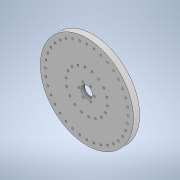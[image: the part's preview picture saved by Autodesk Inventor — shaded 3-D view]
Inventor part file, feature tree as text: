
AUTODESK INVENTOR PART (.ipt)
format: ipt  version: 2020.3 (Build 243373000, 373)  size: 738,304 bytes
history: native  units: mm
features: extrude x12, sketch x12, pattern_circular x4, mirror x1
ambient origin geometry x8: Origin, YZ Plane, XZ Plane, XY Plane, X Axis, Y Axis, Z Axis, Center Point
bodies: Solid1 (feature_tree)
feature tree (29):
  extrude  "Extrusion1"  Depth=40.0mm
  extrude  "Extrusion2"  Depth=7.0mm
  extrude  "Extrusion3"  Depth=180.0mm
  extrude  "Extrusion4"  Depth=5.0mm
  extrude  "Extrusion5"  Depth=7.0mm
  mirror  "Mirror1"
  pattern_circular  "Circular Pattern1"  Count=60 Angle=360.0deg
  extrude  "Extrusion6"  Depth=60.0mm
  pattern_circular  "Circular Pattern2"  [2 undecoded]
  extrude  "Extrusion7"  Depth=60.0mm TaperAngle=360.0deg
  extrude  "Extrusion8"  Depth=60.0mm
  extrude  "Extrusion10"  Depth=60.0mm TaperAngle=0.0deg
  pattern_circular  "Circular Pattern4"  [2 undecoded]
  extrude  "Extrusion12"  Depth=60.0mm
  extrude  "Extrusion13"  Depth=60.0mm
  pattern_circular  "Circular Pattern5"  [2 undecoded]
  extrude  "Extrusion14"  Depth=60.0mm
  sketch  "Sketch1"  dims[d0=40.0mm d1=22.0mm]
  sketch  "Sketch2"  dims[d2=7.0mm d3=0.0mm d4=8.6mm]
  sketch  "Sketch3"  dims[d5=16.0mm d6=0.0mm d7=180.0mm]
  sketch  "Sketch4"  dims[d8=5.0mm d9=0.0mm d10=22.0mm]
  sketch  "Sketch5"  dims[d11=7.0mm d12=0.0mm d14=0.55mm]
  sketch  "Sketch6"  dims[d17=0.4mm]
  sketch  "Sketch7"  dims[d18=0.75mm]
  sketch  "Sketch8"  dims[d19=0.15mm]
  sketch  "Sketch9"  dims[d20=0.523599mm]
  sketch  "Sketch11"  dims[d22=18.8mm]
  sketch  "Sketch12"  dims[d23=8.0mm d24=0.0mm d25=600.0mm d26=360.0deg]
  sketch  "Sketch13"  dims[d28=2.5mm d29=14.0mm d30=23.0mm d31=0.0mm d32=30.0mm d33=360.0deg d35=15.0mm d36=7.2mm d37=0.0mm d38=1.745329mm d39=0.872665mm d40=3.2mm d41=3.2mm d42=3.2mm d43=80.0mm d44=80.0mm d45=40.0mm d46=0.0mm d47=0.0mm d48=120.0deg d49=120.0deg d50=5.7mm d51=120.0deg d52=120.0deg d53=5.7mm d54=29.670597mm d55=120.0deg d60=5.7mm d61=120.0deg d62=120.0deg d63=0.872665mm d69=5.0mm d70=0.0mm d71=180.0mm d72=360.0deg d76=10.0mm d77=0.0mm d78=3.2mm d79=15.0mm d80=10.0mm d81=0.0mm d82=60.0mm d83=360.0deg d85=0.4mm d86=0.0mm d87=0.0mm d74=0.5mm d75=0.872665mm]
note: 6 required parameter values undecoded (feature->parameter linkage not recoverable at this tier; creation-order binding heuristic only, values carry confidence <= 0.55)
